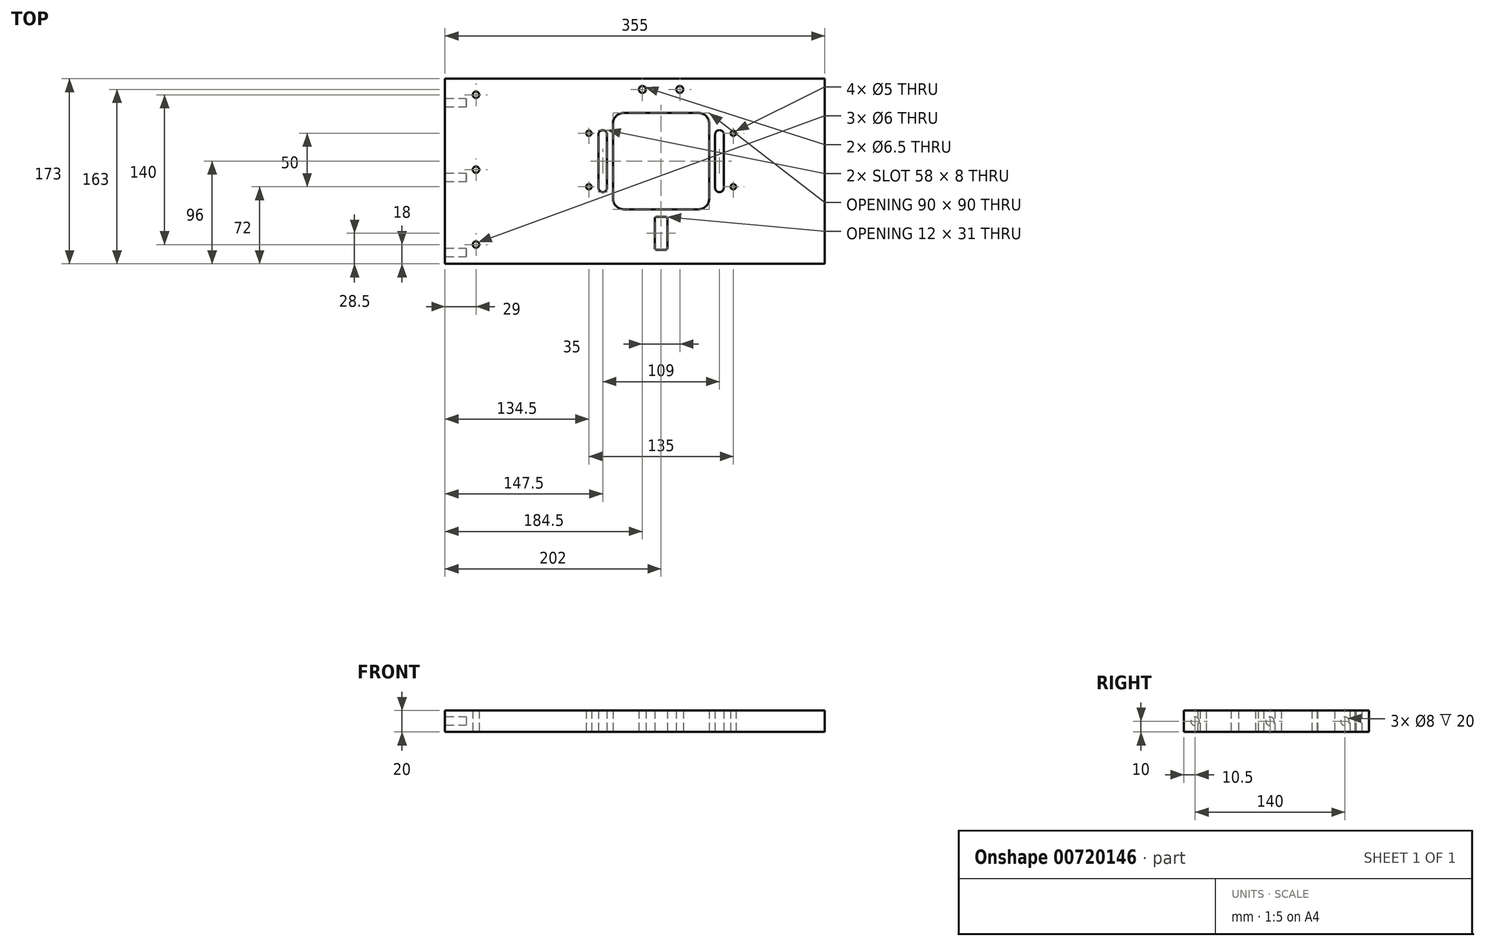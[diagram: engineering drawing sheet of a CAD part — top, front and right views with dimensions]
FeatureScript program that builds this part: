
annotation { "Feature Type Name" : "Feature", "Feature Type Description" : "" }
export const myFeature = defineFeature(function(context is Context, id is Id, definition is map)
    precondition{}
    {
        {
            var Q0;
            Q0=qCreatedBy(makeId("Top.planeOp"),FACE);
            var sketch = newSketch(context, id + "F0", { "sketchPlane" : qUnion([Q0])});
            skLineSegment(sketch, "E0.bottom", {"start": v(0, 0) * mm, "end": v(355, 0) * mm});
            skLineSegment(sketch, "E0.top", {"start": v(0, 173) * mm, "end": v(355, 173) * mm});
            skLineSegment(sketch, "E0.left", {"start": v(0, 0) * mm, "end": v(0, 173) * mm});
            skLineSegment(sketch, "E0.right", {"start": v(355, 0) * mm, "end": v(355, 173) * mm});
            skCircle(sketch, "E1", {"center": v(29, 158) * mm, "radius": 3 * mm});
            skCircle(sketch, "E2.0.1.0", {"center": v(29, 88) * mm, "radius": 3 * mm});
            skCircle(sketch, "E2.0.2.0", {"center": v(29, 18) * mm, "radius": 3 * mm});
            skLineSegment(sketch, "E2.direction1", {"start": v(29, 158) * mm, "end": v(54, 158) * mm, "construction": true});
            skLineSegment(sketch, "E2.direction2", {"start": v(29, 158) * mm, "end": v(29, 88) * mm, "construction": true});
            skCircle(sketch, "E3", {"center": v(134.5, 122) * mm, "radius": 2.5 * mm});
            skCircle(sketch, "E4", {"center": v(134.5, 72) * mm, "radius": 2.5 * mm});
            skCircle(sketch, "E5", {"center": v(269.5, 122) * mm, "radius": 2.5 * mm});
            skCircle(sketch, "E6", {"center": v(269.5, 72) * mm, "radius": 2.5 * mm});
            skCircle(sketch, "E7", {"center": v(184.5, 163) * mm, "radius": 3.25 * mm});
            skCircle(sketch, "E8", {"center": v(219.5, 163) * mm, "radius": 3.25 * mm});
            skLineSegment(sketch, "E9.bottom", {"start": v(167, 51) * mm, "end": v(237, 51) * mm});
            skLineSegment(sketch, "E9.top", {"start": v(167, 141) * mm, "end": v(237, 141) * mm});
            skLineSegment(sketch, "E9.left", {"start": v(157, 61) * mm, "end": v(157, 131) * mm});
            skLineSegment(sketch, "E9.right", {"start": v(247, 61) * mm, "end": v(247, 131) * mm});
            skPoint(sketch, "E10.visualSharp", {"position": v(247, 141) * mm});
            skArc(sketch, "E10.filletArc", {"start": v(247, 131) * mm, "mid": v(244.07, 138.07) * mm, "end": v(237, 141) * mm});
            skPoint(sketch, "E11.visualSharp", {"position": v(157, 141) * mm});
            skArc(sketch, "E11.filletArc", {"start": v(167, 141) * mm, "mid": v(159.93, 138.07) * mm, "end": v(157, 131) * mm});
            skPoint(sketch, "E12.visualSharp", {"position": v(157, 51) * mm});
            skArc(sketch, "E12.filletArc", {"start": v(157, 61) * mm, "mid": v(159.93, 53.93) * mm, "end": v(167, 51) * mm});
            skPoint(sketch, "E13.visualSharp", {"position": v(247, 51) * mm});
            skArc(sketch, "E13.filletArc", {"start": v(237, 51) * mm, "mid": v(244.07, 53.93) * mm, "end": v(247, 61) * mm});
            skLineSegment(sketch, "E14.bottom", {"start": v(198, 13) * mm, "end": v(206, 13) * mm});
            skLineSegment(sketch, "E14.top", {"start": v(198, 44) * mm, "end": v(206, 44) * mm});
            skLineSegment(sketch, "E14.left", {"start": v(196, 15) * mm, "end": v(196, 42) * mm});
            skLineSegment(sketch, "E14.right", {"start": v(208, 15) * mm, "end": v(208, 42) * mm});
            skPoint(sketch, "E15.visualSharp", {"position": v(196, 44) * mm});
            skArc(sketch, "E15.filletArc", {"start": v(198, 44) * mm, "mid": v(196.59, 43.41) * mm, "end": v(196, 42) * mm});
            skPoint(sketch, "E16.visualSharp", {"position": v(208, 44) * mm});
            skArc(sketch, "E16.filletArc", {"start": v(208, 42) * mm, "mid": v(207.41, 43.41) * mm, "end": v(206, 44) * mm});
            skPoint(sketch, "E17.visualSharp", {"position": v(208, 13) * mm});
            skArc(sketch, "E17.filletArc", {"start": v(206, 13) * mm, "mid": v(207.41, 13.59) * mm, "end": v(208, 15) * mm});
            skPoint(sketch, "E18.visualSharp", {"position": v(196, 13) * mm});
            skArc(sketch, "E18.filletArc", {"start": v(196, 15) * mm, "mid": v(196.59, 13.59) * mm, "end": v(198, 13) * mm});
            skLineSegment(sketch, "E19.bottom", {"start": v(256.5, 67) * mm, "end": v(256.5, 67) * mm});
            skLineSegment(sketch, "E19.top", {"start": v(256.5, 125) * mm, "end": v(256.5, 125) * mm});
            skLineSegment(sketch, "E19.left", {"start": v(252.5, 71) * mm, "end": v(252.5, 121) * mm});
            skLineSegment(sketch, "E19.right", {"start": v(260.5, 71) * mm, "end": v(260.5, 121) * mm});
            skPoint(sketch, "E20.visualSharp", {"position": v(252.5, 125) * mm});
            skArc(sketch, "E20.filletArc", {"start": v(256.5, 125) * mm, "mid": v(253.67, 123.83) * mm, "end": v(252.5, 121) * mm});
            skPoint(sketch, "E21.visualSharp", {"position": v(260.5, 125) * mm});
            skArc(sketch, "E21.filletArc", {"start": v(260.5, 121) * mm, "mid": v(259.33, 123.83) * mm, "end": v(256.5, 125) * mm});
            skPoint(sketch, "E22.visualSharp", {"position": v(252.5, 67) * mm});
            skArc(sketch, "E22.filletArc", {"start": v(252.5, 71) * mm, "mid": v(253.67, 68.17) * mm, "end": v(256.5, 67) * mm});
            skPoint(sketch, "E23.visualSharp", {"position": v(260.5, 67) * mm});
            skArc(sketch, "E23.filletArc", {"start": v(256.5, 67) * mm, "mid": v(259.33, 68.17) * mm, "end": v(260.5, 71) * mm});
            skLineSegment(sketch, "E24", {"start": v(202, 141) * mm, "end": v(202, 115.1) * mm, "construction": true});
            skLineSegment(sketch, "E25.MirrorCS", {"start": v(151.5, 71) * mm, "end": v(151.5, 121) * mm});
            skLineSegment(sketch, "E26.MirrorCS", {"start": v(143.5, 71) * mm, "end": v(143.5, 121) * mm});
            skArc(sketch, "E27.MirrorCS", {"start": v(147.5, 67) * mm, "mid": v(144.67, 68.17) * mm, "end": v(143.5, 71) * mm});
            skArc(sketch, "E28.MirrorCS", {"start": v(151.5, 71) * mm, "mid": v(150.33, 68.17) * mm, "end": v(147.5, 67) * mm});
            skArc(sketch, "E29.MirrorCS", {"start": v(143.5, 121) * mm, "mid": v(144.67, 123.83) * mm, "end": v(147.5, 125) * mm});
            skArc(sketch, "E30.MirrorCS", {"start": v(147.5, 125) * mm, "mid": v(150.33, 123.83) * mm, "end": v(151.5, 121) * mm});
            skSolve(sketch);
        }
        {
            var Q0;
            Q0=makeQuery(id+"F0.imprint","IMPRINT",FACE,{"disambiguationData":[TD([[makeQuery(id+"F0.imprint","IMPRINT",EDGE,{"derivedFrom":sQuery(id+"F0.wireOp",EDGE,"E0.bottom")}),1.0]])]});
            extrude(context, id + "F1", {"entities" : qUnion([Q0]), "depth" : 20 * mm, "offsetDistance" : 25 * mm});
        }
        {
            var Q0;
            Q0=makeQuery(id+"F1.opExtrude","SWEPT_FACE",FACE,{"disambiguationData":[OSD([sQuery(id+"F0.wireOp",EDGE,"E0.left")])]});
            var sketch = newSketch(context, id + "F2", { "sketchPlane" : qUnion([Q0])});
            skCircle(sketch, "E31", {"center": v(-150.5, 10) * mm, "radius": 4 * mm});
            skPoint(sketch, "E31.centerSnap0", {"position": v(-173, 10) * mm});
            skCircle(sketch, "E32", {"center": v(-80.5, 10) * mm, "radius": 4 * mm});
            skCircle(sketch, "E33", {"center": v(-10.5, 10) * mm, "radius": 4 * mm});
            skSolve(sketch);
        }
        {
            var Q0;
            Q0=makeQuery(id+"F2.imprint","IMPRINT",FACE,{"disambiguationData":[TD([[makeQuery(id+"F2.imprint","IMPRINT",EDGE,{"derivedFrom":sQuery(id+"F2.wireOp",EDGE,"E31")}),1.0]])]});
            var Q1;
            Q1=makeQuery(id+"F2.imprint","IMPRINT",FACE,{"disambiguationData":[TD([[makeQuery(id+"F2.imprint","IMPRINT",EDGE,{"derivedFrom":sQuery(id+"F2.wireOp",EDGE,"E32")}),1.0]])]});
            var Q2;
            Q2=makeQuery(id+"F2.imprint","IMPRINT",FACE,{"disambiguationData":[TD([[makeQuery(id+"F2.imprint","IMPRINT",EDGE,{"derivedFrom":sQuery(id+"F2.wireOp",EDGE,"E33")}),1.0]])]});
            extrude(context, id + "F3", {"entities" : qUnion([Q0, Q1, Q2]), "operationType" : NewBodyOperationType.REMOVE, "oppositeDirection" : true, "depth" : 20 * mm, "offsetDistance" : 25 * mm});
        }
    });
